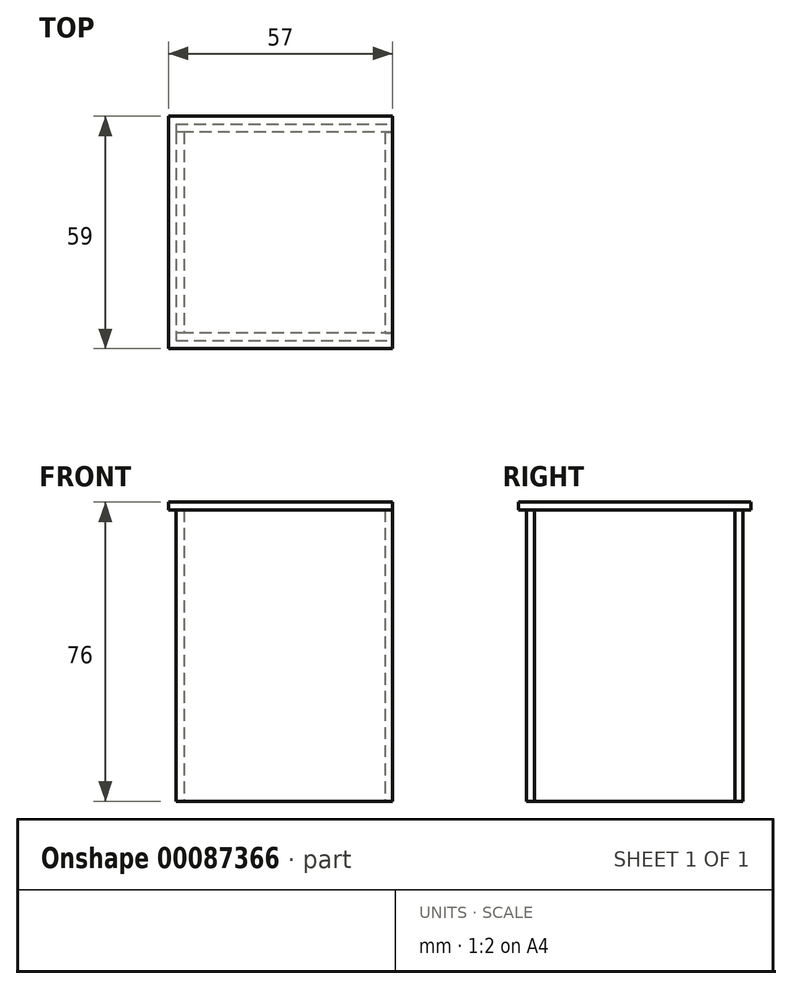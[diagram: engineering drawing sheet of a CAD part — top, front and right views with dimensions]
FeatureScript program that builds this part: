
annotation { "Feature Type Name" : "Feature", "Feature Type Description" : "" }
export const myFeature = defineFeature(function(context is Context, id is Id, definition is map)
    precondition{}
    {
        {
            var Q0;
            Q0=qCreatedBy(makeId("Top.planeOp"),FACE);
            var sketch = newSketch(context, id + "F0", { "sketchPlane" : qUnion([Q0])});
            skLineSegment(sketch, "E0.bottom", {"start": v(-27.5, 27.5) * mm, "end": v(27.5, 27.5) * mm});
            skLineSegment(sketch, "E0.top", {"start": v(-27.5, -27.5) * mm, "end": v(27.5, -27.5) * mm});
            skLineSegment(sketch, "E0.left", {"start": v(-27.5, 27.5) * mm, "end": v(-27.5, -27.5) * mm});
            skLineSegment(sketch, "E0.right", {"start": v(27.5, 27.5) * mm, "end": v(27.5, -27.5) * mm});
            skPoint(sketch, "E0.middle", {"position": v(0, 0) * mm});
            skLineSegment(sketch, "E1.bottom", {"start": v(-25.5, 25.5) * mm, "end": v(25.5, 25.5) * mm});
            skLineSegment(sketch, "E1.top", {"start": v(-25.5, -25.5) * mm, "end": v(25.5, -25.5) * mm});
            skLineSegment(sketch, "E1.left", {"start": v(-25.5, 25.5) * mm, "end": v(-25.5, -25.5) * mm});
            skLineSegment(sketch, "E1.right", {"start": v(25.5, 25.5) * mm, "end": v(25.5, -25.5) * mm});
            skLineSegment(sketch, "E2", {"start": v(-25.5, 25.5) * mm, "end": v(-27.5, 25.5) * mm});
            skLineSegment(sketch, "E3", {"start": v(25.5, 25.5) * mm, "end": v(27.5, 25.5) * mm});
            skLineSegment(sketch, "E4", {"start": v(-25.5, -25.5) * mm, "end": v(-27.5, -25.5) * mm});
            skLineSegment(sketch, "E5", {"start": v(25.5, -25.5) * mm, "end": v(27.5, -25.5) * mm});
            skSolve(sketch);
        }
        {
            var Q0;
            {var subQ1=sQuery(id+"F0.wireOp",EDGE,"E0.bottom");Q0=makeQuery(id+"F0.imprint","IMPRINT",FACE,{"disambiguationData":[TD([[makeQuery(id+"F0.imprint","IMPRINT",EDGE,{"derivedFrom":subQ1}),-1.0]])]});}
            extrude(context, id + "F1", {"entities" : qUnion([Q0]), "depth" : 74 * mm});
        }
        {
            var Q0;
            Q0=makeQuery(id+"F0.imprint","IMPRINT",FACE,{"disambiguationData":[TD([[makeQuery(id+"F0.imprint","IMPRINT",EDGE,{"derivedFrom":sQuery(id+"F0.wireOp",EDGE,"E1.left")}),-1.0]])]});
            extrude(context, id + "F2", {"entities" : qUnion([Q0]), "depth" : 74 * mm});
        }
        {
            var Q0;
            {var subQ1=sQuery(id+"F0.wireOp",EDGE,"E0.top");Q0=makeQuery(id+"F0.imprint","IMPRINT",FACE,{"disambiguationData":[TD([[makeQuery(id+"F0.imprint","IMPRINT",EDGE,{"derivedFrom":subQ1}),1.0]])]});}
            extrude(context, id + "F3", {"entities" : qUnion([Q0]), "depth" : 74 * mm});
        }
        {
            var Q0;
            Q0=makeQuery(id+"F0.imprint","IMPRINT",FACE,{"disambiguationData":[TD([[makeQuery(id+"F0.imprint","IMPRINT",EDGE,{"derivedFrom":sQuery(id+"F0.wireOp",EDGE,"E1.right")}),1.0]])]});
            extrude(context, id + "F4", {"entities" : qUnion([Q0]), "depth" : 74 * mm});
        }
        {
            var Q0;
            Q0=qCreatedBy(makeId("Top.planeOp"),FACE);
            cPlane(context, id + "F5", {"entities" : qUnion([Q0]), "cplaneType" : CPlaneType.OFFSET, "offset" : 74 * mm, "width" : 150 * mm, "height" : 150 * mm});
        }
        {
            var Q0;
            Q0=qCreatedBy(id+"F5.planeOp",FACE);
            var sketch = newSketch(context, id + "F6", { "sketchPlane" : qUnion([Q0])});
            skPoint(sketch, "E6.middle", {"position": v(0, 0) * mm});
            skPoint(sketch, "E7.0", {"position": v(27.5, -27.5) * mm});
            skPoint(sketch, "E8.0", {"position": v(27.5, 27.5) * mm});
            skLineSegment(sketch, "E9", {"start": v(27.5, 27.5) * mm, "end": v(27.5, 29.5) * mm});
            skLineSegment(sketch, "E10", {"start": v(27.5, 29.5) * mm, "end": v(-29.5, 29.5) * mm});
            skLineSegment(sketch, "E11", {"start": v(-29.5, 29.5) * mm, "end": v(-29.5, -29.5) * mm});
            skLineSegment(sketch, "E12", {"start": v(-29.5, -29.5) * mm, "end": v(27.5, -29.5) * mm});
            skLineSegment(sketch, "E13", {"start": v(27.5, -29.5) * mm, "end": v(27.5, -27.5) * mm});
            skLineSegment(sketch, "E14", {"start": v(27.5, 27.5) * mm, "end": v(27.5, -27.5) * mm});
            skSolve(sketch);
        }
        {
            var Q0;
            Q0 = qSketchRegion(id + "F6", true);
            extrude(context, id + "F7", {"entities" : qUnion([Q0]), "depth" : 2 * mm});
        }
    });
